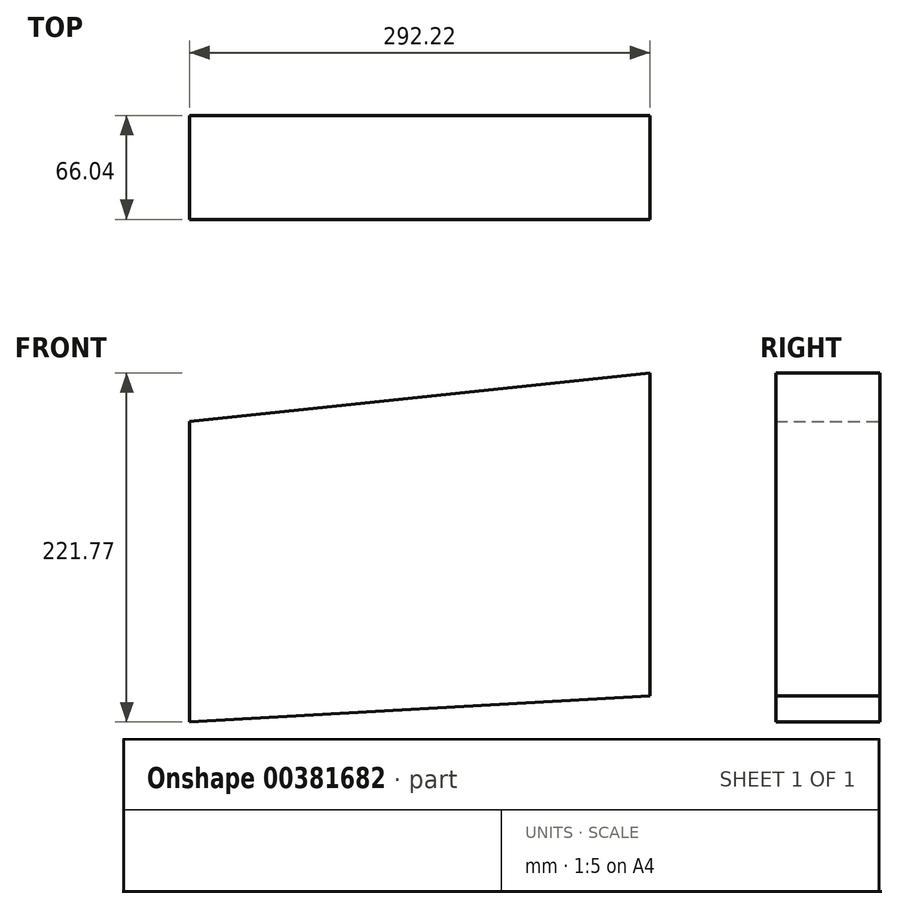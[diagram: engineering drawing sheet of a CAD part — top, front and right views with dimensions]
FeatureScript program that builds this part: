
annotation { "Feature Type Name" : "Feature", "Feature Type Description" : "" }
export const myFeature = defineFeature(function(context is Context, id is Id, definition is map)
    precondition{}
    {
        {
            var Q0;
            Q0=qCreatedBy(makeId("Front.planeOp"),FACE);
            var sketch = newSketch(context, id + "F0", { "sketchPlane" : qUnion([Q0])});
            skLineSegment(sketch, "E0", {"start": v(107.76, 119.82) * mm, "end": v(-184.46, 88.84) * mm});
            skLineSegment(sketch, "E1", {"start": v(-184.46, 88.84) * mm, "end": v(-184.46, -101.95) * mm});
            skLineSegment(sketch, "E2", {"start": v(-184.46, -101.95) * mm, "end": v(107.76, -85.41) * mm});
            skLineSegment(sketch, "E3", {"start": v(107.76, -62) * mm, "end": v(107.76, -85.41) * mm});
            skLineSegment(sketch, "E4", {"start": v(107.76, -62) * mm, "end": v(107.76, 119.82) * mm});
            skSolve(sketch);
        }
        {
            var Q0;
            Q0 = qSketchRegion(id + "F0", true);
            extrude(context, id + "F1", {"entities" : qUnion([Q0]), "depth" : 66.04 * mm});
        }
    });
